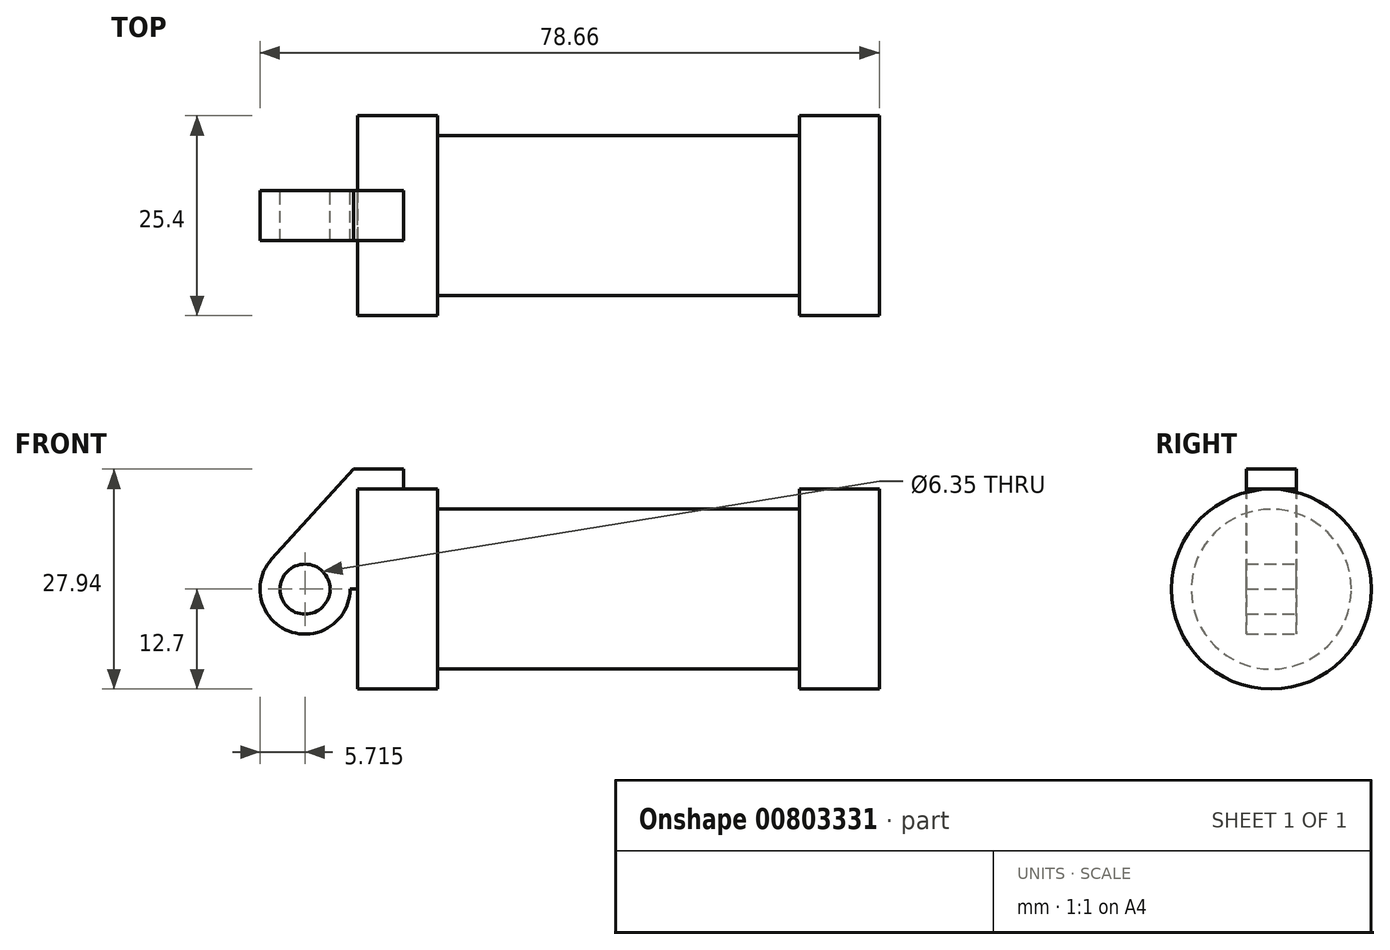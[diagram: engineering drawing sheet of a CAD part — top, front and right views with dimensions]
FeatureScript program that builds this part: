
annotation { "Feature Type Name" : "Feature", "Feature Type Description" : "" }
export const myFeature = defineFeature(function(context is Context, id is Id, definition is map)
    precondition{}
    {
        {
            var Q0;
            Q0=qCreatedBy(makeId("Front.planeOp"),FACE);
            var sketch = newSketch(context, id + "F0", { "sketchPlane" : qUnion([Q0])});
            skLineSegment(sketch, "E0", {"start": v(0, 0) * mm, "end": v(0, 12.7) * mm});
            skLineSegment(sketch, "E1", {"start": v(0, 12.7) * mm, "end": v(10.16, 12.7) * mm});
            skLineSegment(sketch, "E2", {"start": v(10.16, 12.7) * mm, "end": v(10.16, 10.16) * mm});
            skLineSegment(sketch, "E3", {"start": v(10.16, 10.16) * mm, "end": v(56.13, 10.16) * mm});
            skLineSegment(sketch, "E4", {"start": v(56.13, 10.16) * mm, "end": v(56.13, 12.7) * mm});
            skLineSegment(sketch, "E5", {"start": v(56.13, 12.7) * mm, "end": v(66.3, 12.7) * mm});
            skLineSegment(sketch, "E6", {"start": v(66.3, 12.7) * mm, "end": v(66.3, 0) * mm});
            skLineSegment(sketch, "E7", {"start": v(66.3, 0) * mm, "end": v(0, 0) * mm});
            skLineSegment(sketch, "E8", {"start": v(5.84, 15.24) * mm, "end": v(-0.5, 15.24) * mm});
            skLineSegment(sketch, "E9", {"start": v(-0.5, 15.24) * mm, "end": v(-10.88, 3.85) * mm});
            skLineSegment(sketch, "E10", {"start": v(0, 0) * mm, "end": v(-6.65, 0) * mm});
            skCircle(sketch, "E11", {"center": v(-6.65, 0) * mm, "radius": 5.72 * mm});
            skCircle(sketch, "E12", {"center": v(-6.65, 0) * mm, "radius": 3.18 * mm});
            skLineSegment(sketch, "E13", {"start": v(5.84, 15.24) * mm, "end": v(5.84, -9.4) * mm});
            skLineSegment(sketch, "E14", {"start": v(5.84, -9.4) * mm, "end": v(-8.18, -5.5) * mm});
            skSolve(sketch);
        }
        {
            var Q0;
            {var subQ1=sQuery(id+"F0.wireOp",EDGE,"E0");Q0=makeQuery(id+"F0.imprint","IMPRINT",FACE,{"disambiguationData":[TD([[makeQuery(id+"F0.imprint","IMPRINT",EDGE,{"derivedFrom":subQ1}),1.0]])]});}
            var Q1;
            {var subQ5=sQuery(id+"F0.wireOp",EDGE,"E12");Q1=makeQuery(id+"F0.imprint","IMPRINT",FACE,{"disambiguationData":[TD([[makeQuery(id+"F0.imprint","IMPRINT",EDGE,{"derivedFrom":subQ5}),-1.0]])]});}
            extrude(context, id + "F1", {"entities" : qUnion([Q0, Q1]), "endBound" : BoundingType.SYMMETRIC, "depth" : 6.35 * mm, "offsetDistance" : 25.4 * mm});
        }
        {
            var Q0;
            {var subQ0=sQuery(id+"F0.wireOp",EDGE,"E2");Q0=makeQuery(id+"F0.imprint","IMPRINT",FACE,{"disambiguationData":[TD([[makeQuery(id+"F0.imprint","IMPRINT",EDGE,{"derivedFrom":subQ0}),-1.0]])]});}
            var Q1;
            {var subQ0=sQuery(id+"F0.wireOp",EDGE,"E0");Q1=makeQuery(id+"F0.imprint","IMPRINT",FACE,{"disambiguationData":[TD([[makeQuery(id+"F0.imprint","IMPRINT",EDGE,{"derivedFrom":subQ0}),-1.0]])]});}
            var Q2;
            Q2=sQuery(id+"F0.wireOp",EDGE,"E7");
            revolve(context, id + "F2", {"surfaceOperationType" : NewSurfaceOperationType.NEW, "entities" : qUnion([Q0, Q1]), "axis" : qUnion([Q2]), "revolveType" : RevolveType.FULL});
        }
    });
